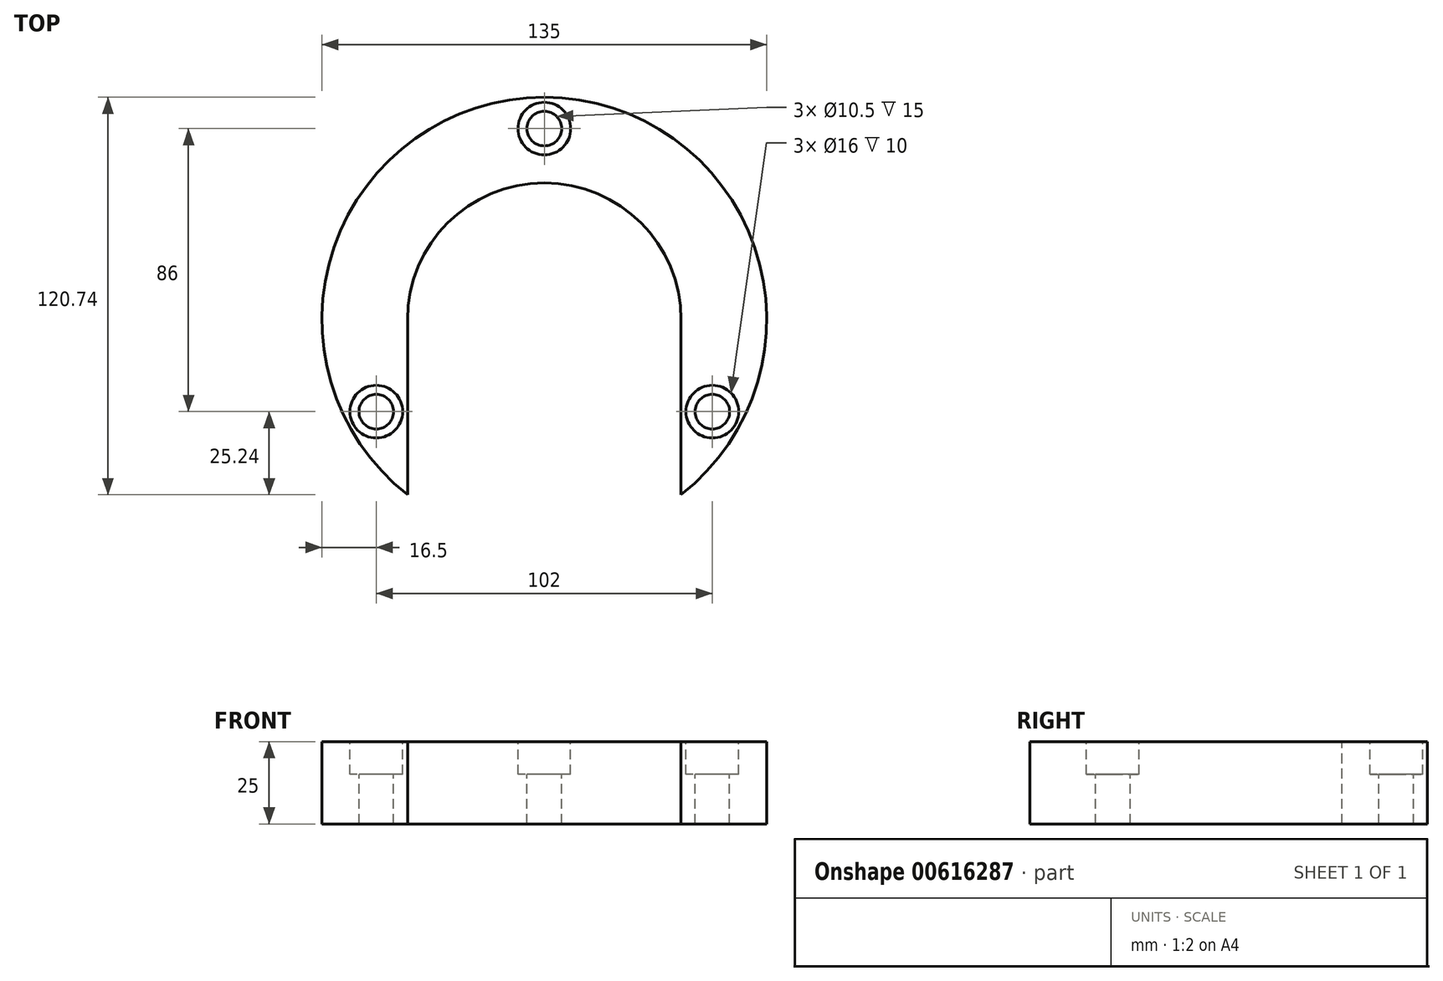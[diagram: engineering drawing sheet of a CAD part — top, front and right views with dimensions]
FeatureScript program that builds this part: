
annotation { "Feature Type Name" : "Feature", "Feature Type Description" : "" }
export const myFeature = defineFeature(function(context is Context, id is Id, definition is map)
    precondition{}
    {
        {
            var Q0;
            Q0=qCreatedBy(makeId("Top.planeOp"),FACE);
            var sketch = newSketch(context, id + "F0", { "sketchPlane" : qUnion([Q0])});
            skCircle(sketch, "E0", {"center": v(0, 0) * mm, "radius": 67.5 * mm});
            skSolve(sketch);
        }
        {
            var Q0;
            Q0=makeQuery(id+"F0.imprint","IMPRINT",FACE,{"disambiguationData":[TD([[makeQuery(id+"F0.imprint","IMPRINT",EDGE,{"derivedFrom":sQuery(id+"F0.wireOp",EDGE,"E0")}),1.0]])]});
            extrude(context, id + "F1", {"entities" : qUnion([Q0]), "depth" : 25 * mm, "offsetDistance" : 25 * mm});
        }
        {
            var Q0;
            Q0=makeQuery(id+"F1.opExtrude","CAP_FACE",FACE,{"disambiguationData":[OSD([sQuery(id+"F0.wireOp",EDGE,"E0")])],"isStart":false});
            var sketch = newSketch(context, id + "F2", { "sketchPlane" : qUnion([Q0])});
            skCircle(sketch, "E1", {"center": v(0, 0) * mm, "radius": 41.5 * mm});
            skLineSegment(sketch, "E2", {"start": v(-41.5, 0) * mm, "end": v(-41.5, -53.24) * mm});
            skLineSegment(sketch, "E3", {"start": v(41.5, 0) * mm, "end": v(41.5, -53.24) * mm});
            skSolve(sketch);
        }
        {
            var Q0;
            {var subQ0=sQuery(id+"F2.wireOp",EDGE,"E1");var subQ1=makeQuery(id+"F2.imprint","INTERSECT",VERTEX,{"derivedFrom":[subQ0,sQuery(id+"F2.wireOp",EDGE,"E2")]});Q0=makeQuery(id+"F2.imprint","IMPRINT",FACE,{"disambiguationData":[TD([[makeQuery(id+"F2.imprint","IMPRINT",EDGE,{"disambiguationData":[TD([[subQ1,1.0]])],"derivedFrom":subQ0}),1.0]])]});}
            var Q1;
            {var subQ0=sQuery(id+"F2.wireOp",EDGE,"E2");Q1=makeQuery(id+"F2.imprint","IMPRINT",FACE,{"disambiguationData":[TD([[makeQuery(id+"F2.imprint","IMPRINT",EDGE,{"derivedFrom":subQ0}),1.0]])]});}
            extrude(context, id + "F3", {"entities" : qUnion([Q0, Q1]), "operationType" : NewBodyOperationType.REMOVE, "endBound" : BoundingType.THROUGH_ALL, "oppositeDirection" : true, "depth" : 25 * mm, "offsetDistance" : 25 * mm});
        }
        {
            var Q0;
            Q0=makeQuery(id+"F1.opExtrude","CAP_FACE",FACE,{"disambiguationData":[OSD([sQuery(id+"F0.wireOp",EDGE,"E0")])],"isStart":false});
            var sketch = newSketch(context, id + "F4", { "sketchPlane" : qUnion([Q0])});
            skCircle(sketch, "E4", {"center": v(0, 58) * mm, "radius": 5.25 * mm});
            skCircle(sketch, "E5", {"center": v(-51, -28) * mm, "radius": 5.25 * mm});
            skCircle(sketch, "E6", {"center": v(51, -28) * mm, "radius": 5.25 * mm});
            skCircle(sketch, "E7", {"center": v(-51, -28) * mm, "radius": 8 * mm});
            skCircle(sketch, "E8", {"center": v(51, -28) * mm, "radius": 8 * mm});
            skCircle(sketch, "E9", {"center": v(0, 58) * mm, "radius": 8 * mm});
            skSolve(sketch);
        }
        {
            var Q0;
            Q0=makeQuery(id+"F4.imprint","IMPRINT",FACE,{"disambiguationData":[TD([[makeQuery(id+"F4.imprint","IMPRINT",EDGE,{"derivedFrom":sQuery(id+"F4.wireOp",EDGE,"E6")}),1.0]])]});
            var Q1;
            Q1=makeQuery(id+"F4.imprint","IMPRINT",FACE,{"disambiguationData":[TD([[makeQuery(id+"F4.imprint","IMPRINT",EDGE,{"derivedFrom":sQuery(id+"F4.wireOp",EDGE,"E5")}),1.0]])]});
            var Q2;
            Q2=makeQuery(id+"F4.imprint","IMPRINT",FACE,{"disambiguationData":[TD([[makeQuery(id+"F4.imprint","IMPRINT",EDGE,{"derivedFrom":sQuery(id+"F4.wireOp",EDGE,"E4")}),1.0]])]});
            extrude(context, id + "F5", {"entities" : qUnion([Q0, Q1, Q2]), "operationType" : NewBodyOperationType.REMOVE, "endBound" : BoundingType.THROUGH_ALL, "oppositeDirection" : true, "depth" : 25 * mm, "offsetDistance" : 25 * mm});
        }
        {
            var Q0;
            Q0=makeQuery(id+"F4.imprint","IMPRINT",FACE,{"disambiguationData":[TD([[makeQuery(id+"F4.imprint","IMPRINT",EDGE,{"derivedFrom":sQuery(id+"F4.wireOp",EDGE,"E6")}),-1.0]])]});
            var Q1;
            Q1=makeQuery(id+"F4.imprint","IMPRINT",FACE,{"disambiguationData":[TD([[makeQuery(id+"F4.imprint","IMPRINT",EDGE,{"derivedFrom":sQuery(id+"F4.wireOp",EDGE,"E4")}),-1.0]])]});
            var Q2;
            Q2=makeQuery(id+"F4.imprint","IMPRINT",FACE,{"disambiguationData":[TD([[makeQuery(id+"F4.imprint","IMPRINT",EDGE,{"derivedFrom":sQuery(id+"F4.wireOp",EDGE,"E5")}),-1.0]])]});
            extrude(context, id + "F6", {"entities" : qUnion([Q0, Q1, Q2]), "operationType" : NewBodyOperationType.REMOVE, "oppositeDirection" : true, "depth" : 10 * mm, "offsetDistance" : 25 * mm});
        }
    });
